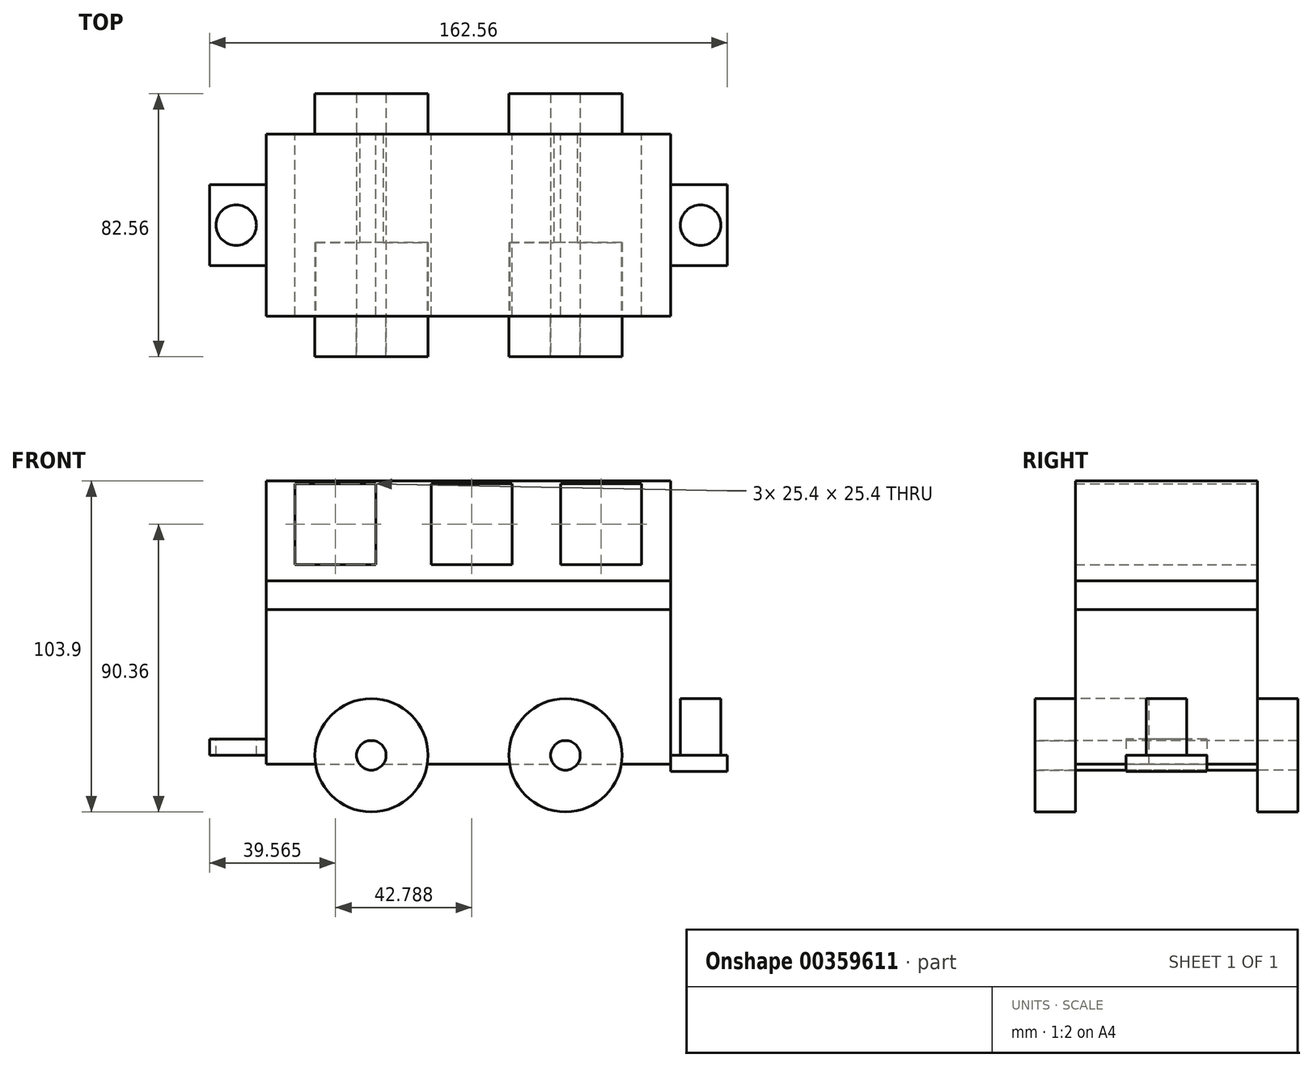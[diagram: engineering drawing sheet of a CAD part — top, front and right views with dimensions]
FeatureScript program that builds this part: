
annotation { "Feature Type Name" : "Feature", "Feature Type Description" : "" }
export const myFeature = defineFeature(function(context is Context, id is Id, definition is map)
    precondition{}
    {
        {
            var Q0;
            Q0=qCreatedBy(makeId("Front.planeOp"),FACE);
            var sketch = newSketch(context, id + "F0", { "sketchPlane" : qUnion([Q0])});
            skLineSegment(sketch, "E0.bottom", {"start": v(-57.6, 68.94) * mm, "end": v(69.4, 68.94) * mm});
            skLineSegment(sketch, "E0.top", {"start": v(-57.6, -19.96) * mm, "end": v(69.4, -19.96) * mm});
            skLineSegment(sketch, "E0.left", {"start": v(-57.6, 68.94) * mm, "end": v(-57.6, -19.96) * mm});
            skLineSegment(sketch, "E0.right", {"start": v(69.4, 68.94) * mm, "end": v(69.4, -19.96) * mm});
            skLineSegment(sketch, "E1", {"start": v(-57.6, 37.62) * mm, "end": v(69.4, 37.62) * mm});
            skLineSegment(sketch, "E2", {"start": v(-57.6, 28.5) * mm, "end": v(69.4, 28.5) * mm});
            skLineSegment(sketch, "E3.bottom", {"start": v(-48.51, 68.1) * mm, "end": v(-23.11, 68.1) * mm});
            skLineSegment(sketch, "E3.top", {"start": v(-48.51, 42.7) * mm, "end": v(-23.11, 42.7) * mm});
            skLineSegment(sketch, "E3.left", {"start": v(-48.51, 68.1) * mm, "end": v(-48.51, 42.7) * mm});
            skLineSegment(sketch, "E3.right", {"start": v(-23.11, 68.1) * mm, "end": v(-23.11, 42.7) * mm});
            skLineSegment(sketch, "E4.bottom", {"start": v(60.31, 68.1) * mm, "end": v(34.91, 68.1) * mm});
            skLineSegment(sketch, "E4.top", {"start": v(60.31, 42.7) * mm, "end": v(34.91, 42.7) * mm});
            skLineSegment(sketch, "E4.left", {"start": v(60.31, 68.1) * mm, "end": v(60.31, 42.7) * mm});
            skLineSegment(sketch, "E4.right", {"start": v(34.91, 68.1) * mm, "end": v(34.91, 42.7) * mm});
            skLineSegment(sketch, "E5.bottom", {"start": v(-5.73, 68.1) * mm, "end": v(19.67, 68.1) * mm});
            skLineSegment(sketch, "E5.top", {"start": v(-5.73, 42.7) * mm, "end": v(19.67, 42.7) * mm});
            skLineSegment(sketch, "E5.left", {"start": v(-5.73, 68.1) * mm, "end": v(-5.73, 42.7) * mm});
            skLineSegment(sketch, "E5.right", {"start": v(19.67, 68.1) * mm, "end": v(19.67, 42.7) * mm});
            skSolve(sketch);
        }
        {
            var Q0;
            {var subQ0=sQuery(id+"F0.wireOp",EDGE,"E0.bottom");Q0=makeQuery(id+"F0.imprint","IMPRINT",FACE,{"disambiguationData":[TD([[makeQuery(id+"F0.imprint","IMPRINT",EDGE,{"derivedFrom":subQ0}),-1.0]])]});}
            var Q1;
            {var subQ8=sQuery(id+"F0.wireOp",EDGE,"E2");Q1=makeQuery(id+"F0.imprint","IMPRINT",FACE,{"disambiguationData":[TD([[makeQuery(id+"F0.imprint","IMPRINT",EDGE,{"derivedFrom":subQ8}),-1.0]])]});}
            extrude(context, id + "F1", {"entities" : qUnion([Q0, Q1]), "endBound" : BoundingType.SYMMETRIC, "depth" : 57.15 * mm});
        }
        {
            var Q0;
            {var subQ0=sQuery(id+"F0.wireOp",EDGE,"E1");Q0=makeQuery(id+"F0.imprint","IMPRINT",FACE,{"disambiguationData":[TD([[makeQuery(id+"F0.imprint","IMPRINT",EDGE,{"derivedFrom":subQ0}),-1.0]])]});}
            extrude(context, id + "F2", {"entities" : qUnion([Q0]), "endBound" : BoundingType.SYMMETRIC, "depth" : 57.15 * mm});
        }
        {
            var Q0;
            Q0=makeQuery(id+"F1.opExtrude","CAP_FACE",FACE,{"disambiguationData":[OSD([sQuery(id+"F0.wireOp",EDGE,"E0.top"),sQuery(id+"F0.wireOp",EDGE,"E0.left"),sQuery(id+"F0.wireOp",EDGE,"E0.right"),sQuery(id+"F0.wireOp",EDGE,"E2")])],"isStart":false});
            var sketch = newSketch(context, id + "F3", { "sketchPlane" : qUnion([Q0])});
            skCircle(sketch, "E6", {"center": v(-24.58, -17.18) * mm, "radius": 17.78 * mm});
            skCircle(sketch, "E7", {"center": v(36.38, -17.18) * mm, "radius": 17.78 * mm});
            skCircle(sketch, "E8", {"center": v(-24.58, -17.18) * mm, "radius": 4.65 * mm});
            skCircle(sketch, "E9", {"center": v(36.38, -17.18) * mm, "radius": 4.65 * mm});
            skSolve(sketch);
        }
        {
            var Q0;
            {var subQ0=sQuery(id+"F3.wireOp",EDGE,"E6");var subQ1=makeQuery(id+"F1.opExtrude","CAP_EDGE",EDGE,{"disambiguationData":[OSD([sQuery(id+"F0.wireOp",EDGE,"E0.top")])],"isStart":false});var subQ2=makeQuery(id+"F3.imprint","INTERSECT",VERTEX,{"disambiguationData":[OD(0.0)],"derivedFrom":[subQ1,subQ0]});Q0=makeQuery(id+"F3.imprint","IMPRINT",FACE,{"disambiguationData":[TD([[makeQuery(id+"F3.imprint","IMPRINT",EDGE,{"disambiguationData":[TD([[subQ2,-1.0]])],"derivedFrom":subQ0}),1.0]])]});}
            var Q1;
            {var subQ0=sQuery(id+"F3.wireOp",EDGE,"E6");var subQ1=makeQuery(id+"F1.opExtrude","CAP_EDGE",EDGE,{"disambiguationData":[OSD([sQuery(id+"F0.wireOp",EDGE,"E0.top")])],"isStart":false});var subQ2=makeQuery(id+"F3.imprint","INTERSECT",VERTEX,{"disambiguationData":[OD(0.0)],"derivedFrom":[subQ1,subQ0]});Q1=makeQuery(id+"F3.imprint","IMPRINT",FACE,{"disambiguationData":[TD([[makeQuery(id+"F3.imprint","IMPRINT",EDGE,{"disambiguationData":[TD([[subQ2,1.0]])],"derivedFrom":subQ0}),1.0]])]});}
            var Q2;
            {var subQ0=sQuery(id+"F3.wireOp",EDGE,"E7");var subQ1=makeQuery(id+"F1.opExtrude","CAP_EDGE",EDGE,{"disambiguationData":[OSD([sQuery(id+"F0.wireOp",EDGE,"E0.top")])],"isStart":false});var subQ2=makeQuery(id+"F3.imprint","INTERSECT",VERTEX,{"disambiguationData":[OD(0.0)],"derivedFrom":[subQ1,subQ0]});Q2=makeQuery(id+"F3.imprint","IMPRINT",FACE,{"disambiguationData":[TD([[makeQuery(id+"F3.imprint","IMPRINT",EDGE,{"disambiguationData":[TD([[subQ2,-1.0]])],"derivedFrom":subQ0}),1.0]])]});}
            var Q3;
            {var subQ0=sQuery(id+"F3.wireOp",EDGE,"E7");var subQ1=makeQuery(id+"F1.opExtrude","CAP_EDGE",EDGE,{"disambiguationData":[OSD([sQuery(id+"F0.wireOp",EDGE,"E0.top")])],"isStart":false});var subQ2=makeQuery(id+"F3.imprint","INTERSECT",VERTEX,{"disambiguationData":[OD(0.0)],"derivedFrom":[subQ1,subQ0]});Q3=makeQuery(id+"F3.imprint","IMPRINT",FACE,{"disambiguationData":[TD([[makeQuery(id+"F3.imprint","IMPRINT",EDGE,{"disambiguationData":[TD([[subQ2,1.0]])],"derivedFrom":subQ0}),1.0]])]});}
            extrude(context, id + "F4", {"entities" : qUnion([Q0, Q1, Q2, Q3]), "depth" : 12.7 * mm});
        }
        {
            var Q0;
            Q0=makeQuery(id+"F4.opExtrude","SWEPT_BODY",BODY,{"disambiguationData":[OSD([sQuery(id+"F3.wireOp",EDGE,"E6")])]});
            var Q1;
            Q1=makeQuery(id+"F4.opExtrude","SWEPT_BODY",BODY,{"disambiguationData":[OSD([sQuery(id+"F3.wireOp",EDGE,"E7")])]});
            var Q2;
            Q2=qCreatedBy(makeId("Front.planeOp"),FACE);
            mirror(context, id + "F5", {"operationType" : NewBodyOperationType.ADD, "entities" : qUnion([Q0, Q1]), "mirrorPlane" : qUnion([Q2])});
        }
        {
            var Q0;
            Q0 = qSketchRegion(id + "F3", true);
            extrude(context, id + "F6", {"entities" : qUnion([Q0]), "operationType" : NewBodyOperationType.REMOVE, "oppositeDirection" : true, "depth" : 23.1 * mm});
        }
        {
            var Q0;
            Q0=makeQuery(id+"F3.imprint","IMPRINT",FACE,{"disambiguationData":[TD([[makeQuery(id+"F3.imprint","IMPRINT",EDGE,{"derivedFrom":sQuery(id+"F3.wireOp",EDGE,"E9")}),1.0]])]});
            var Q1;
            Q1=makeQuery(id+"F3.imprint","IMPRINT",FACE,{"disambiguationData":[TD([[makeQuery(id+"F3.imprint","IMPRINT",EDGE,{"derivedFrom":sQuery(id+"F3.wireOp",EDGE,"E8")}),1.0]])]});
            var Q2;
            Q2=sQuery(id+"F3.wireOp",EDGE,"E8");
            var Q3;
            Q3=sQuery(id+"F3.wireOp",EDGE,"E9");
            extrude(context, id + "F7", {"entities" : qUnion([Q0, Q1]), "operationType" : NewBodyOperationType.REMOVE, "surfaceEntities" : qUnion([Q2, Q3]), "oppositeDirection" : true, "depth" : 82.8 * mm, "hasSecondDirection" : true, "secondDirectionOppositeDirection" : false, "secondDirectionDepth" : 76.2 * mm});
        }
        {
            var Q0;
            Q0=makeQuery(id+"F3.imprint","IMPRINT",FACE,{"disambiguationData":[TD([[makeQuery(id+"F3.imprint","IMPRINT",EDGE,{"derivedFrom":sQuery(id+"F3.wireOp",EDGE,"E8")}),1.0]])]});
            var Q1;
            Q1=makeQuery(id+"F3.imprint","IMPRINT",FACE,{"disambiguationData":[TD([[makeQuery(id+"F3.imprint","IMPRINT",EDGE,{"derivedFrom":sQuery(id+"F3.wireOp",EDGE,"E9")}),1.0]])]});
            var Q2;
            Q2=sQuery(id+"F3.wireOp",EDGE,"E9");
            var Q3;
            Q3=sQuery(id+"F3.wireOp",EDGE,"E8");
            extrude(context, id + "F8", {"entities" : qUnion([Q0, Q1]), "surfaceEntities" : qUnion([Q2, Q3]), "oppositeDirection" : true, "depth" : 69.85 * mm, "hasSecondDirection" : true, "secondDirectionOppositeDirection" : false, "secondDirectionDepth" : 12.7 * mm});
        }
        {
            var Q0;
            {var subQ0=sQuery(id+"F0.wireOp",EDGE,"E0.right");Q0=makeQuery(id+"F1.opExtrude","SWEPT_FACE",FACE,{"disambiguationData":[OSD([subQ0]),TDD([makeQuery(id+"F0.imprint","IMPRINT",EDGE,{"disambiguationData":[TD([[makeQuery(id+"F0.imprint","INTERSECT",VERTEX,{"derivedFrom":[sQuery(id+"F0.wireOp",EDGE,"E0.top"),subQ0]}),1.0]])],"derivedFrom":subQ0})])]});}
            var sketch = newSketch(context, id + "F9", { "sketchPlane" : qUnion([Q0])});
            skLineSegment(sketch, "E10.bottom", {"start": v(-12.7, -17.22) * mm, "end": v(12.7, -17.22) * mm});
            skLineSegment(sketch, "E10.top", {"start": v(-12.7, -22.3) * mm, "end": v(12.7, -22.3) * mm});
            skLineSegment(sketch, "E10.left", {"start": v(-12.7, -17.22) * mm, "end": v(-12.7, -22.3) * mm});
            skLineSegment(sketch, "E10.right", {"start": v(12.7, -17.22) * mm, "end": v(12.7, -22.3) * mm});
            skSolve(sketch);
        }
        {
            var Q0;
            Q0 = qSketchRegion(id + "F9", true);
            extrude(context, id + "F10", {"entities" : qUnion([Q0]), "operationType" : NewBodyOperationType.ADD, "depth" : 17.78 * mm});
        }
        {
            var Q0;
            Q0=makeQuery(id+"F10.opExtrude","SWEPT_FACE",FACE,{"disambiguationData":[OSD([sQuery(id+"F9.wireOp",EDGE,"E10.bottom")])]});
            var sketch = newSketch(context, id + "F11", { "sketchPlane" : qUnion([Q0])});
            skCircle(sketch, "E11", {"center": v(78.82, 0) * mm, "radius": 6.35 * mm});
            skSolve(sketch);
        }
        {
            var Q0;
            Q0 = qSketchRegion(id + "F11", true);
            extrude(context, id + "F12", {"entities" : qUnion([Q0]), "operationType" : NewBodyOperationType.ADD, "depth" : 17.78 * mm});
        }
        {
            var Q0;
            {var subQ0=sQuery(id+"F0.wireOp",EDGE,"E0.left");Q0=makeQuery(id+"F1.opExtrude","SWEPT_FACE",FACE,{"disambiguationData":[OSD([subQ0]),TDD([makeQuery(id+"F0.imprint","IMPRINT",EDGE,{"disambiguationData":[TD([[makeQuery(id+"F0.imprint","INTERSECT",VERTEX,{"derivedFrom":[sQuery(id+"F0.wireOp",EDGE,"E0.top"),subQ0]}),1.0]])],"derivedFrom":subQ0})])]});}
            var sketch = newSketch(context, id + "F13", { "sketchPlane" : qUnion([Q0])});
            skLineSegment(sketch, "E12.bottom", {"start": v(-12.7, -12.14) * mm, "end": v(12.7, -12.14) * mm});
            skLineSegment(sketch, "E12.top", {"start": v(-12.7, -17.22) * mm, "end": v(12.7, -17.22) * mm});
            skLineSegment(sketch, "E12.left", {"start": v(-12.7, -12.14) * mm, "end": v(-12.7, -17.22) * mm});
            skLineSegment(sketch, "E12.right", {"start": v(12.7, -12.14) * mm, "end": v(12.7, -17.22) * mm});
            skSolve(sketch);
        }
        {
            var Q0;
            Q0 = qSketchRegion(id + "F13", true);
            extrude(context, id + "F14", {"entities" : qUnion([Q0]), "operationType" : NewBodyOperationType.ADD, "depth" : 17.78 * mm});
        }
        {
            var Q0;
            Q0=makeQuery(id+"F14.opExtrude","SWEPT_FACE",FACE,{"disambiguationData":[OSD([sQuery(id+"F13.wireOp",EDGE,"E12.bottom")])]});
            var sketch = newSketch(context, id + "F15", { "sketchPlane" : qUnion([Q0])});
            skCircle(sketch, "E13", {"center": v(-67.02, 0) * mm, "radius": 6.35 * mm});
            skSolve(sketch);
        }
        {
            var Q0;
            Q0 = qSketchRegion(id + "F15", true);
            extrude(context, id + "F16", {"entities" : qUnion([Q0]), "operationType" : NewBodyOperationType.REMOVE, "oppositeDirection" : true, "depth" : 25.4 * mm});
        }
    });
